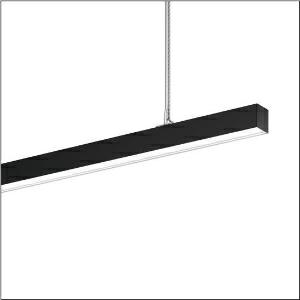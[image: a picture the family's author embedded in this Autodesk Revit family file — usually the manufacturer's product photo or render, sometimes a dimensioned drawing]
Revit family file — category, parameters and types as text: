
# Revit family: silica_r__21_51mx30tbt5b_11dd
name_source: partatom
category: Lighting Fixtures
units: mm (PartAtom-declared; Revit-internal decimal feet)

## family parameters
Cut with Voids When Loaded = No
Host = Face
Light Source = No
Part Type = Normal
Room Calculation Point = No
Round Connector Dimension = Use Diameter
Shared = No

## types (1)
- --- (1 x LED, 5150 lm, 42.2 W, 6500K)
    Apparent Load = 42 VA
    CIE Flux Codes = 47 79 96 58 100
    Color Rendering = 80
    Color Temperature = 6500K
    Default Elevation = 1800 mm
    Description = Silica® 21, office luminaire, primary optical cover: cover, of PMMA, opal, light emission: direct/indirect distribution, primary light characteristic: symmetric, installation type: suspended mounting, LED, rated luminous flux: 5.150lm, luminous efficacy: 116lm/W, light colour: 8tw, colour temperature: 2700..6500K, control gear: ECG DALI, with terminal, 3+2-pole, max. 2.5mm², mains connection: 220..240V, AC, 50/60Hz, rated input power: 44.3W, luminaire housing, of aluminium, jet black (RAL 9005), length: 1.504mm, width: 53mm, height: 53mm, protection rating (complete): IP20, insulation class (complete): insulation class I (protective earthing), certification: CE, permissible operating ambient temperature: 0..+35°C, standard: EN 50419, packaging unit: 1 piece
    Height = 53 mm
    Lamp = 1 x LED
    Lamp Light Flux = 5150 lm
    Lamp Power = 42.2 W
    Lamp count = 1
    Length = 1504 mm
    Luminous efficacy = 122 lm/W
    Manufacturer = Siteco
    ModVariant = No
    Model = 51MX30TBT5B
    Mounting Place = Ceiling
    Mounting Type = Pendant
    Number of Poles = 1
    OnlyDefault = Yes
    Power Factor = 1
    Product Name = Silica® 21
    Product group = office luminaire | ceiling pendant
    ProductGroupID = 902
    Protection Class = Protection class I
    Protection Degree = IP 20
    RLX_Detail_Level = 1
    RLX_Emergency_Light_Flux = 0 lm
    RLX_Emergency_Type = 0
    RLX_Emergency_Type_DB = No
    RlxData = <blob elided: 22881 chars, md5=cf263734>
    Socket = socket
    Standby Power = 0 W
    System Light Flux = 5150 lm
    System Power = 42 W
    Type Comments = individual setting
    Type Image = l_1313646.jpg
    URL = http://relux.com
    VarID = @adj_089001
    Voltage = 0 V
    Weight = 0.00 kg
    Width = 53 mm

## geometry (parser evidence)
native form markers: Blend x4, Sweep x11
no freeform markers — native parametric forms only
